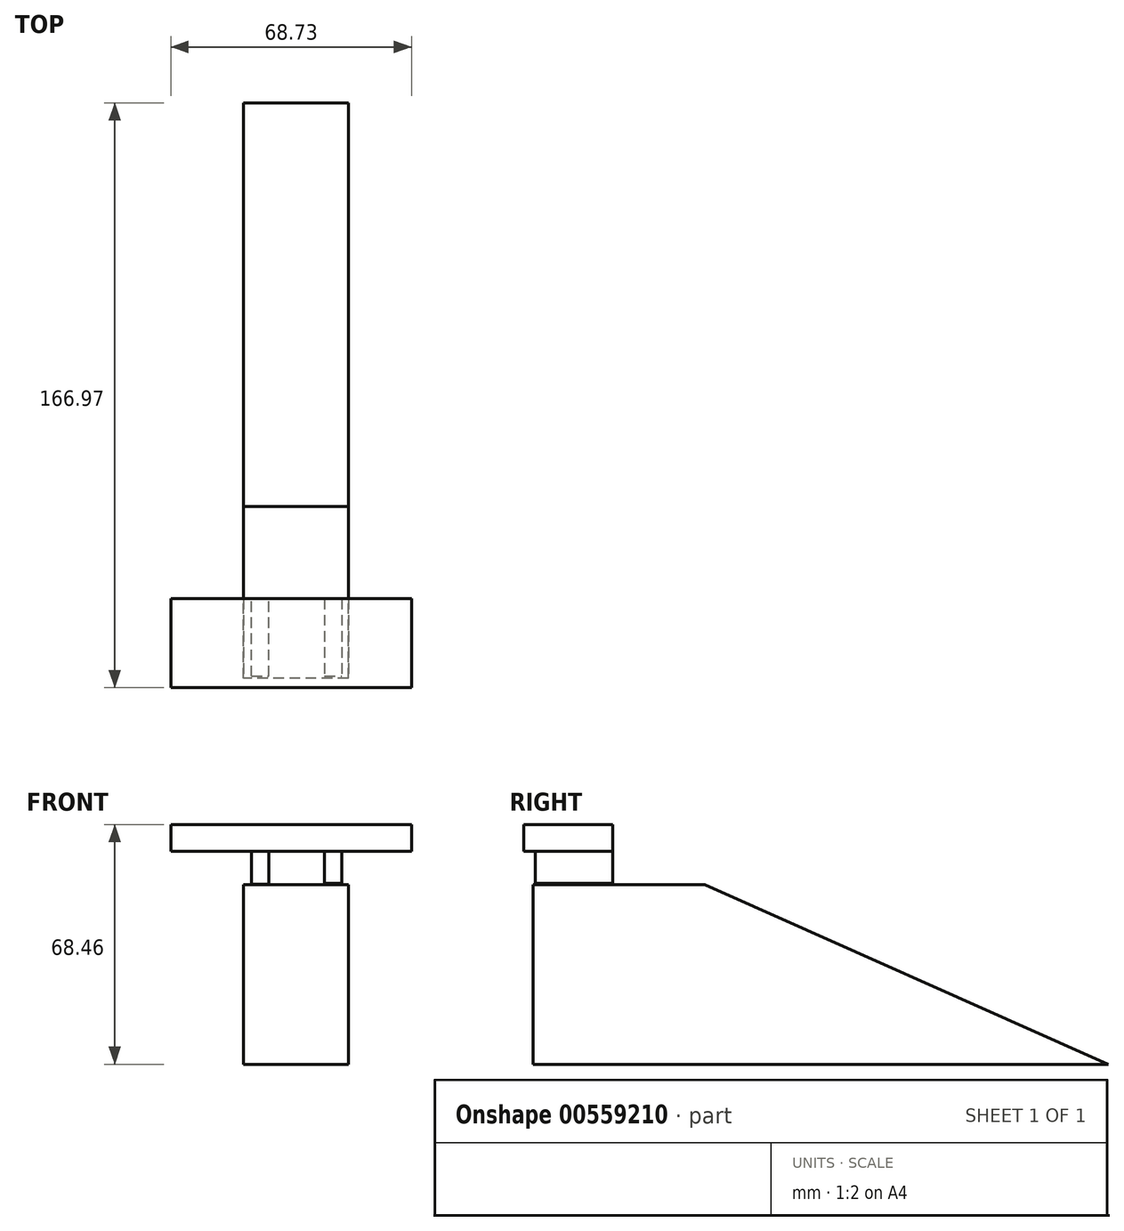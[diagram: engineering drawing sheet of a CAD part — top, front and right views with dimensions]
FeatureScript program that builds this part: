
annotation { "Feature Type Name" : "Feature", "Feature Type Description" : "" }
export const myFeature = defineFeature(function(context is Context, id is Id, definition is map)
    precondition{}
    {
        {
            var Q0;
            Q0=qCreatedBy(makeId("Right.planeOp"),FACE);
            var sketch = newSketch(context, id + "F0", { "sketchPlane" : qUnion([Q0])});
            skLineSegment(sketch, "E0", {"start": v(-96.37, 22.67) * mm, "end": v(-96.37, -28.64) * mm});
            skLineSegment(sketch, "E1", {"start": v(-96.37, -28.64) * mm, "end": v(67.9, -28.64) * mm});
            skLineSegment(sketch, "E2", {"start": v(67.9, -28.64) * mm, "end": v(-47.27, 22.67) * mm});
            skLineSegment(sketch, "E3", {"start": v(-47.27, 22.67) * mm, "end": v(-96.37, 22.67) * mm});
            skSolve(sketch);
        }
        {
            var Q0;
            Q0=makeQuery(id+"F0.imprint","IMPRINT",FACE,{"disambiguationData":[TD([[makeQuery(id+"F0.imprint","IMPRINT",EDGE,{"derivedFrom":sQuery(id+"F0.wireOp",EDGE,"E0")}),1.0]])]});
            extrude(context, id + "F1", {"entities" : qUnion([Q0]), "depth" : 30 * mm, "offsetDistance" : 25.4 * mm});
        }
        {
            var Q0;
            Q0=qCreatedBy(makeId("Front.planeOp"),FACE);
            cPlane(context, id + "F2", {"entities" : qUnion([Q0]), "cplaneType" : CPlaneType.OFFSET, "offset" : 73.66 * mm, "width" : 152.4 * mm, "height" : 152.4 * mm});
        }
        {
            var Q0;
            Q0=qCreatedBy(id+"F2.planeOp",FACE);
            var sketch = newSketch(context, id + "F3", { "sketchPlane" : qUnion([Q0])});
            skLineSegment(sketch, "E4.bottom", {"start": v(-20.72, 39.82) * mm, "end": v(48, 39.82) * mm});
            skLineSegment(sketch, "E4.top", {"start": v(-20.72, 32.13) * mm, "end": v(48, 32.13) * mm});
            skLineSegment(sketch, "E4.left", {"start": v(-20.72, 39.82) * mm, "end": v(-20.72, 32.13) * mm});
            skLineSegment(sketch, "E4.right", {"start": v(48, 39.82) * mm, "end": v(48, 32.13) * mm});
            skSolve(sketch);
        }
        {
            var Q0;
            Q0 = qSketchRegion(id + "F3", true);
            extrude(context, id + "F4", {"entities" : qUnion([Q0]), "depth" : 25.4 * mm, "offsetDistance" : 25.4 * mm});
        }
        {
            var Q0;
            Q0=qCreatedBy(id+"F2.planeOp",FACE);
            var sketch = newSketch(context, id + "F5", { "sketchPlane" : qUnion([Q0])});
            skLineSegment(sketch, "E5.bottom", {"start": v(2.36, 32.37) * mm, "end": v(7.32, 32.37) * mm});
            skLineSegment(sketch, "E5.top", {"start": v(2.36, 22.7) * mm, "end": v(7.32, 22.7) * mm});
            skLineSegment(sketch, "E5.left", {"start": v(2.36, 32.37) * mm, "end": v(2.36, 22.7) * mm});
            skLineSegment(sketch, "E5.right", {"start": v(7.32, 32.37) * mm, "end": v(7.32, 22.7) * mm});
            skLineSegment(sketch, "E6.bottom", {"start": v(28.16, 22.95) * mm, "end": v(23.2, 22.95) * mm});
            skLineSegment(sketch, "E6.top", {"start": v(28.16, 32.37) * mm, "end": v(23.2, 32.37) * mm});
            skLineSegment(sketch, "E6.left", {"start": v(28.16, 22.95) * mm, "end": v(28.16, 32.37) * mm});
            skLineSegment(sketch, "E6.right", {"start": v(23.2, 22.95) * mm, "end": v(23.2, 32.37) * mm});
            skSolve(sketch);
        }
        {
            var Q0;
            Q0 = qSketchRegion(id + "F5", true);
            extrude(context, id + "F6", {"entities" : qUnion([Q0]), "operationType" : NewBodyOperationType.ADD, "depth" : 22.1 * mm, "offsetDistance" : 25.4 * mm});
        }
    });
